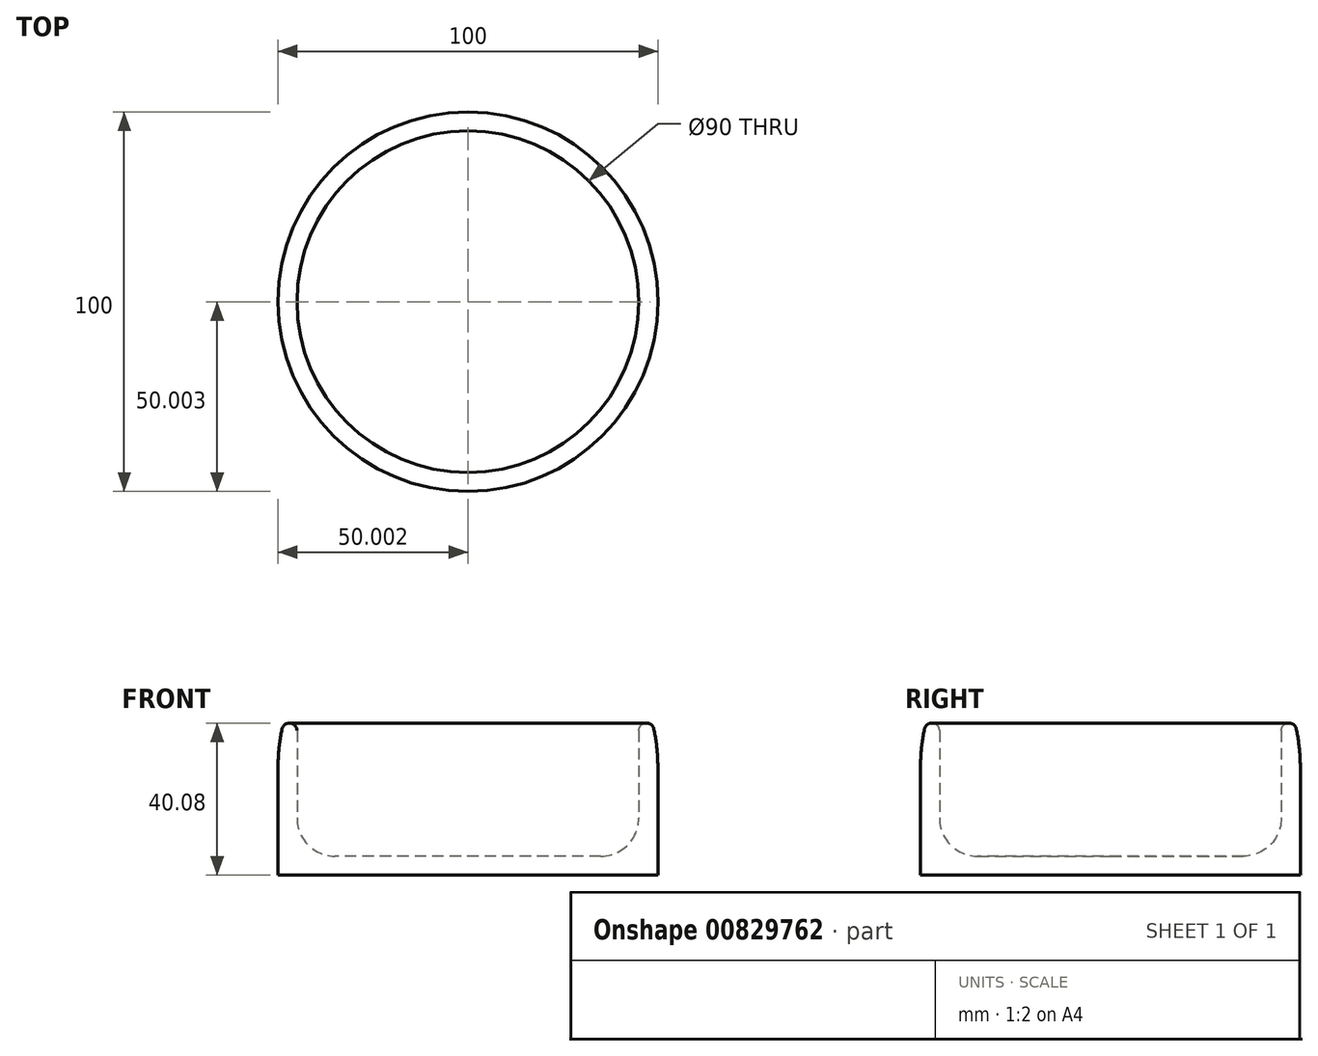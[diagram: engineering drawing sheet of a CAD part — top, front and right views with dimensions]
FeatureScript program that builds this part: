
annotation { "Feature Type Name" : "Feature", "Feature Type Description" : "" }
export const myFeature = defineFeature(function(context is Context, id is Id, definition is map)
    precondition{}
    {
        {
            var Q0;
            Q0=qCreatedBy(makeId("Top.planeOp"),FACE);
            var sketch = newSketch(context, id + "F0", { "sketchPlane" : qUnion([Q0])});
            skCircle(sketch, "E0", {"center": v(-0.06, 0.34) * mm, "radius": 50 * mm});
            skSolve(sketch);
        }
        {
            var Q0;
            Q0 = qSketchRegion(id + "F0", true);
            extrude(context, id + "F1", {"entities" : qUnion([Q0]), "depth" : 50 * mm, "offsetDistance" : 25 * mm});
        }
        {
            var Q0;
            Q0=makeQuery(id+"F1.opExtrude","CAP_FACE",FACE,{"disambiguationData":[OSD([sQuery(id+"F0.wireOp",EDGE,"E0")])],"isStart":false});
            shell(context, id + "F2", {"entities" : qUnion([Q0]), "thickness" : 5 * mm});
        }
        {
            var Q0;
            Q0=makeQuery(id+"F1.opExtrude","CAP_EDGE",EDGE,{"disambiguationData":[OSD([sQuery(id+"F0.wireOp",EDGE,"E0")])],"isStart":false});
            fillet(context, id + "F3", {"entities" : qUnion([Q0]), "radius" : 49 * mm, "tangentPropagation" : true, "allowEdgeOverflow" : false});
        }
        {
            var Q0;
            {var subQ0=sQuery(id+"F0.wireOp",EDGE,"E0");Q0=makeQuery(id+"F3.opFillet","BLEND_EDGE",EDGE,{"blendedFrom":[makeQuery(id+"F1.opExtrude","CAP_EDGE",EDGE,{"disambiguationData":[OSD([subQ0])],"isStart":false}),makeQuery(id+"F2.opShell","OFFSET_FACE",FACE,{"disambiguationData":[OSD([subQ0]),TDD([makeQuery(id+"F1.opExtrude","SWEPT_FACE",FACE,{"disambiguationData":[OSD([subQ0])]})])]})],"blendedInto":[makeQuery(id+"F2.opShell","OFFSET_FACE",FACE,{"disambiguationData":[OSD([subQ0]),TDD([makeQuery(id+"F1.opExtrude","SWEPT_FACE",FACE,{"disambiguationData":[OSD([subQ0])]})])]})]});}
            fillet(context, id + "F4", {"entities" : qUnion([Q0]), "radius" : 2 * mm, "tangentPropagation" : true, "allowEdgeOverflow" : false});
        }
        {
            var Q0;
            {var subQ0=sQuery(id+"F0.wireOp",EDGE,"E0");Q0=makeQuery(id+"F2.opShell","OFFSET_FACE",FACE,{"disambiguationData":[OSD([subQ0]),TDD([makeQuery(id+"F1.opExtrude","CAP_FACE",FACE,{"disambiguationData":[OSD([subQ0])],"isStart":true})])]});}
            fillet(context, id + "F5", {"entities" : qUnion([Q0]), "radius" : 10 * mm, "tangentPropagation" : true, "allowEdgeOverflow" : false});
        }
    });
